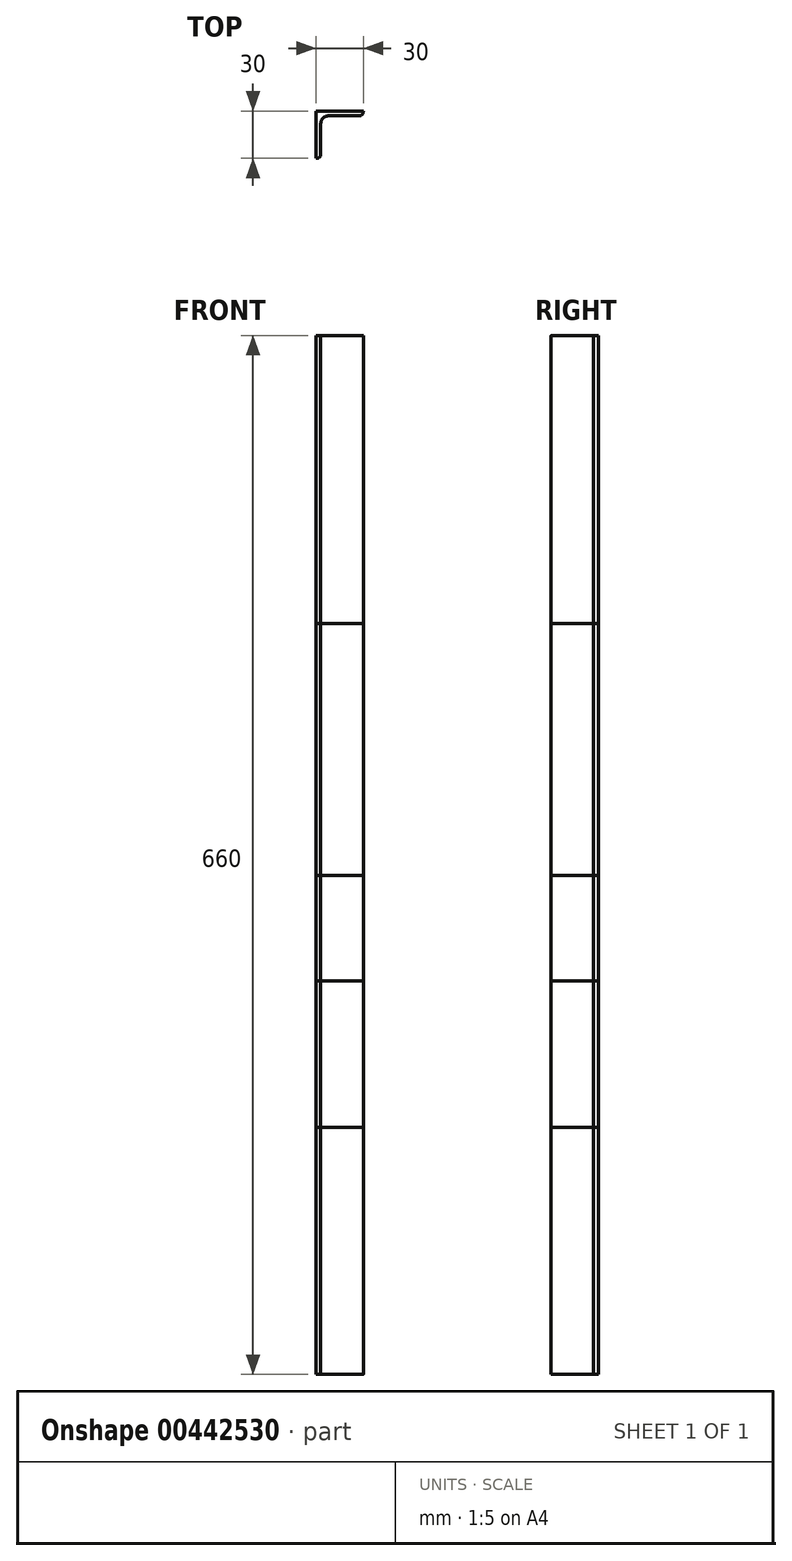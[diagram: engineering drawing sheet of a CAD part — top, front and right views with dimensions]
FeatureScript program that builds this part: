
annotation { "Feature Type Name" : "Feature", "Feature Type Description" : "" }
export const myFeature = defineFeature(function(context is Context, id is Id, definition is map)
    precondition{}
    {
        {
            assignVariable(context, id + "F0", {"name" : "ProfileDepth", "anyValue" : 3 * mm});
        }
        {
            assignVariable(context, id + "F1", {"name" : "Height", "anyValue" : 480 * mm});
        }
        {
            assignVariable(context, id + "F2", {"name" : "StepWidth", "anyValue" : 250 * mm});
        }
        {
            assignVariable(context, id + "F3", {"name" : "StairsWidth", "anyValue" : 660 * mm});
        }
        {
            var Q0;
            Q0=qCreatedBy(makeId("Top.planeOp"),FACE);
            var sketch = newSketch(context, id + "F4", { "sketchPlane" : qUnion([Q0])});
            skLineSegment(sketch, "E0", {"start": v(0, 0) * mm, "end": v(30, 0) * mm});
            skLineSegment(sketch, "E1", {"start": v(27.5, -3) * mm, "end": v(8, -3) * mm});
            skLineSegment(sketch, "E2", {"start": v(3, -8) * mm, "end": v(3, -27.5) * mm});
            skLineSegment(sketch, "E3", {"start": v(0.5, -30) * mm, "end": v(0, -30) * mm});
            skLineSegment(sketch, "E4", {"start": v(0, -30) * mm, "end": v(0, 0) * mm});
            skLineSegment(sketch, "E5", {"start": v(30, -0.5) * mm, "end": v(30, 0) * mm});
            skPoint(sketch, "E6.visualSharp", {"position": v(3, -30) * mm});
            skArc(sketch, "E6.filletArc", {"start": v(0.5, -30) * mm, "mid": v(2.27, -29.27) * mm, "end": v(3, -27.5) * mm});
            skPoint(sketch, "E7.visualSharp", {"position": v(30, -3) * mm});
            skArc(sketch, "E7.filletArc", {"start": v(27.5, -3) * mm, "mid": v(29.27, -2.27) * mm, "end": v(30, -0.5) * mm});
            skPoint(sketch, "E8.visualSharp", {"position": v(3, -3) * mm});
            skArc(sketch, "E8.filletArc", {"start": v(8, -3) * mm, "mid": v(4.46, -4.46) * mm, "end": v(3, -8) * mm});
            skSolve(sketch);
        }
        {
            var Q0;
            Q0=makeQuery(id+"F4.imprint","IMPRINT",FACE,{"disambiguationData":[TD([[makeQuery(id+"F4.imprint","IMPRINT",EDGE,{"derivedFrom":sQuery(id+"F4.wireOp",EDGE,"E0")}),-1.0]])]});
            extrude(context, id + "F5", {"entities" : qUnion([Q0]), "depth" : getVariable(context, 'StairsWidth')});
        }
        {
            var Q0;
            Q0 = qSketchRegion(id + "F4", true);
            extrude(context, id + "F6", {"entities" : qUnion([Q0]), "depth" : getVariable(context, 'Height') - getVariable(context, 'ProfileDepth')});
        }
        {
            var Q0;
            Q0 = qSketchRegion(id + "F4", true);
            extrude(context, id + "F7", {"entities" : qUnion([Q0]), "depth" : 2 / 3 * getVariable(context, 'Height') - getVariable(context, 'ProfileDepth')});
        }
        {
            var Q0;
            Q0 = qSketchRegion(id + "F4", true);
            extrude(context, id + "F8", {"entities" : qUnion([Q0]), "depth" : 1 / 3 * getVariable(context, 'Height') - getVariable(context, 'ProfileDepth')});
        }
        {
            var Q0;
            Q0 = qSketchRegion(id + "F4", true);
            extrude(context, id + "F9", {"entities" : qUnion([Q0]), "depth" : getVariable(context, 'StepWidth')});
        }
    });
